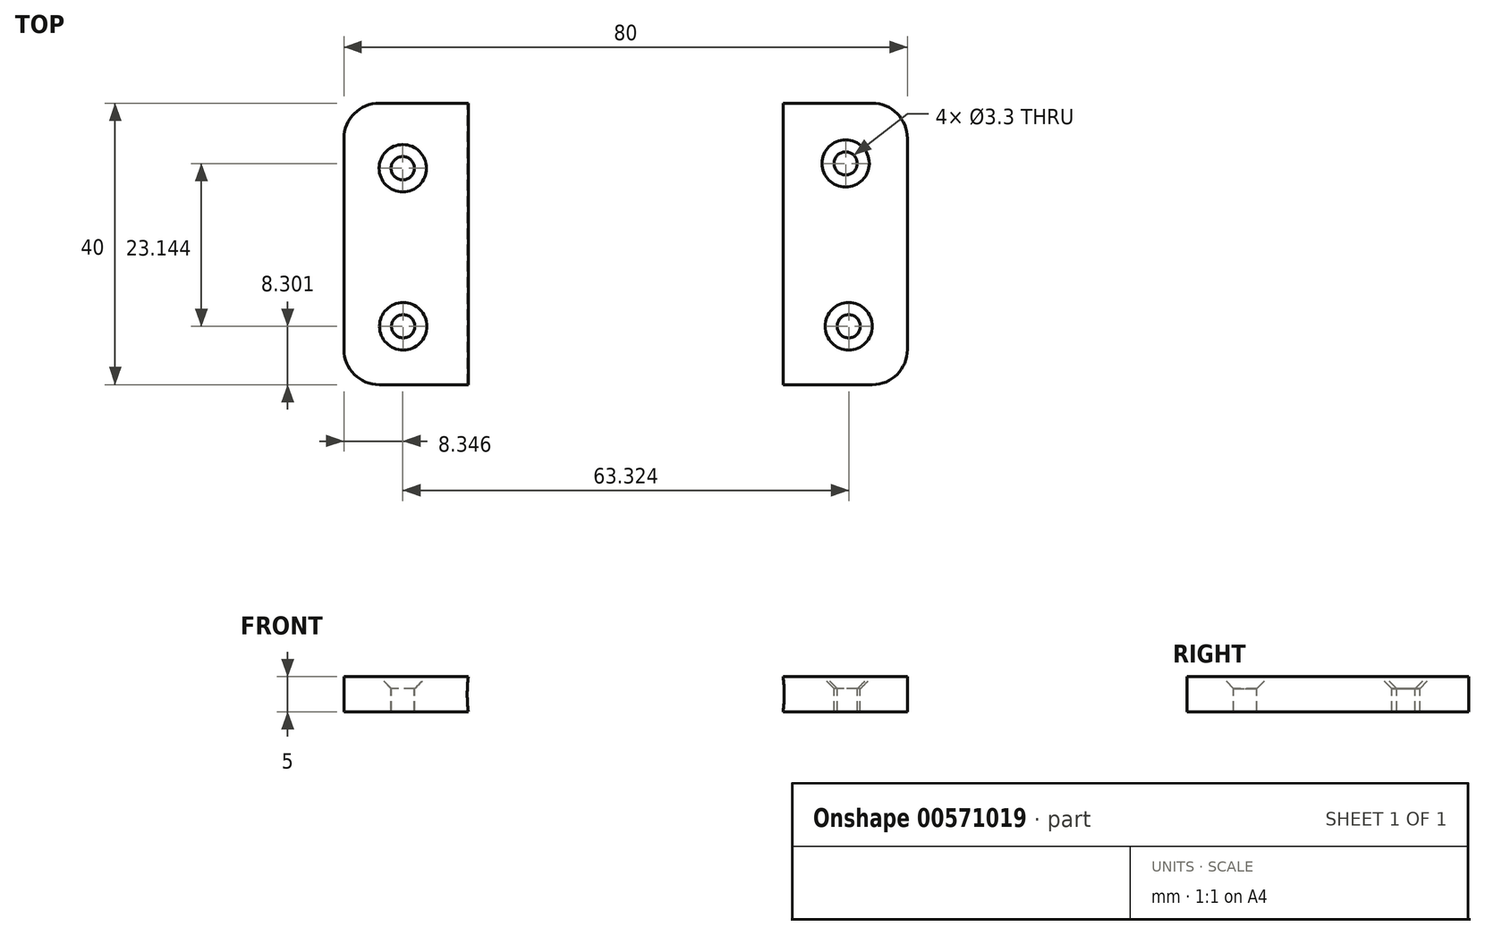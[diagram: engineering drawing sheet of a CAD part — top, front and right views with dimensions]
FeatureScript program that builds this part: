
annotation { "Feature Type Name" : "Feature", "Feature Type Description" : "" }
export const myFeature = defineFeature(function(context is Context, id is Id, definition is map)
    precondition{}
    {
        {
            var Q0;
            Q0=qCreatedBy(makeId("Front.planeOp"),FACE);
            var sketch = newSketch(context, id + "F0", { "sketchPlane" : qUnion([Q0])});
            skLineSegment(sketch, "E0.bottom", {"start": v(40, -2.5) * mm, "end": v(-40, -2.5) * mm});
            skLineSegment(sketch, "E0.top", {"start": v(40, 2.5) * mm, "end": v(-40, 2.5) * mm});
            skLineSegment(sketch, "E0.left", {"start": v(40, -2.5) * mm, "end": v(40, 2.5) * mm});
            skLineSegment(sketch, "E0.right", {"start": v(-40, -2.5) * mm, "end": v(-40, 2.5) * mm});
            skPoint(sketch, "E0.middle", {"position": v(0, 0) * mm});
            skCircle(sketch, "E1", {"center": v(0, 0) * mm, "radius": 22.5 * mm});
            skCircle(sketch, "E2", {"center": v(0, 0) * mm, "radius": 17.5 * mm});
            skSolve(sketch);
        }
        {
            var Q0;
            {var subQ0=sQuery(id+"F0.wireOp",EDGE,"E0.right");Q0=makeQuery(id+"F0.imprint","IMPRINT",FACE,{"disambiguationData":[TD([[makeQuery(id+"F0.imprint","IMPRINT",EDGE,{"derivedFrom":subQ0}),-1.0]])]});}
            var Q1;
            {var subQ0=sQuery(id+"F0.wireOp",EDGE,"E1");var subQ1=sQuery(id+"F0.wireOp",EDGE,"E0.bottom");var subQ2=makeQuery(id+"F0.imprint","INTERSECT",VERTEX,{"disambiguationData":[OD(1.0)],"derivedFrom":[subQ1,subQ0]});Q1=makeQuery(id+"F0.imprint","IMPRINT",FACE,{"disambiguationData":[TD([[makeQuery(id+"F0.imprint","IMPRINT",EDGE,{"disambiguationData":[TD([[subQ2,1.0]])],"derivedFrom":subQ1}),-1.0]])]});}
            var Q2;
            {var subQ0=sQuery(id+"F0.wireOp",EDGE,"E1");var subQ1=sQuery(id+"F0.wireOp",EDGE,"E0.top");var subQ2=makeQuery(id+"F0.imprint","INTERSECT",VERTEX,{"disambiguationData":[OD(0.0)],"derivedFrom":[subQ1,subQ0]});Q2=makeQuery(id+"F0.imprint","IMPRINT",FACE,{"disambiguationData":[TD([[makeQuery(id+"F0.imprint","IMPRINT",EDGE,{"disambiguationData":[TD([[subQ2,-1.0]])],"derivedFrom":subQ1}),-1.0]])]});}
            var Q3;
            {var subQ0=sQuery(id+"F0.wireOp",EDGE,"E1");var subQ1=sQuery(id+"F0.wireOp",EDGE,"E0.bottom");var subQ2=makeQuery(id+"F0.imprint","INTERSECT",VERTEX,{"disambiguationData":[OD(0.0)],"derivedFrom":[subQ1,subQ0]});Q3=makeQuery(id+"F0.imprint","IMPRINT",FACE,{"disambiguationData":[TD([[makeQuery(id+"F0.imprint","IMPRINT",EDGE,{"disambiguationData":[TD([[subQ2,-1.0]])],"derivedFrom":subQ1}),-1.0]])]});}
            var Q4;
            {var subQ0=sQuery(id+"F0.wireOp",EDGE,"E0.left");Q4=makeQuery(id+"F0.imprint","IMPRINT",FACE,{"disambiguationData":[TD([[makeQuery(id+"F0.imprint","IMPRINT",EDGE,{"derivedFrom":subQ0}),1.0]])]});}
            extrude(context, id + "F1", {"entities" : qUnion([Q0, Q1, Q2, Q3, Q4]), "depth" : 40 * mm, "offsetDistance" : 25 * mm});
        }
        {
            var Q0;
            Q0=makeQuery(id+"F1.opExtrude","CAP_EDGE",EDGE,{"disambiguationData":[OSD([sQuery(id+"F0.wireOp",EDGE,"E0.right")])],"isStart":false});
            var Q1;
            Q1=makeQuery(id+"F1.opExtrude","CAP_EDGE",EDGE,{"disambiguationData":[OSD([sQuery(id+"F0.wireOp",EDGE,"E0.right")])],"isStart":true});
            var Q2;
            Q2=makeQuery(id+"F1.opExtrude","CAP_EDGE",EDGE,{"disambiguationData":[OSD([sQuery(id+"F0.wireOp",EDGE,"E0.left")])],"isStart":false});
            var Q3;
            Q3=makeQuery(id+"F1.opExtrude","CAP_EDGE",EDGE,{"disambiguationData":[OSD([sQuery(id+"F0.wireOp",EDGE,"E0.left")])],"isStart":true});
            fillet(context, id + "F2", {"entities" : qUnion([Q0, Q1, Q2, Q3]), "radius" : 5 * mm, "tangentPropagation" : true, "allowEdgeOverflow" : false});
        }
        {
            var Q0;
            {var subQ0=sQuery(id+"F0.wireOp",EDGE,"E0.top");Q0=makeQuery(id+"F1.opExtrude","SWEPT_FACE",FACE,{"disambiguationData":[OSD([subQ0]),TDD([makeQuery(id+"F0.imprint","IMPRINT",EDGE,{"disambiguationData":[TD([[makeQuery(id+"F0.imprint","INTERSECT",VERTEX,{"derivedFrom":[subQ0,sQuery(id+"F0.wireOp",EDGE,"E0.right")]}),1.0]])],"derivedFrom":subQ0})])]});}
            var sketch = newSketch(context, id + "F3", { "sketchPlane" : qUnion([Q0])});
            skPoint(sketch, "E3", {"position": v(-31.65, -9.23) * mm});
            skPoint(sketch, "E4", {"position": v(-31.6, -31.7) * mm});
            skPoint(sketch, "E5", {"position": v(31.23, -8.56) * mm});
            skPoint(sketch, "E6", {"position": v(31.67, -31.7) * mm});
            skSolve(sketch);
        }
        {
            var Q0;
            Q0=sQuery(id+"F3.wireOp",VERTEX,"E3");
            var Q1;
            Q1=sQuery(id+"F3.wireOp",VERTEX,"E4");
            var Q2;
            Q2=sQuery(id+"F3.wireOp",VERTEX,"E5");
            var Q3;
            Q3=sQuery(id+"F3.wireOp",VERTEX,"E6");
            var Q4;
            Q4=makeQuery(id+"F1.opExtrude","SWEPT_BODY",BODY,{"disambiguationData":[OSD([sQuery(id+"F0.wireOp",EDGE,"E0.bottom"),sQuery(id+"F0.wireOp",EDGE,"E0.top"),sQuery(id+"F0.wireOp",EDGE,"E0.left"),sQuery(id+"F0.wireOp",EDGE,"E0.right"),sQuery(id+"F0.wireOp",EDGE,"E1"),sQuery(id+"F0.wireOp",EDGE,"E2")])]});
            hole(context, id + "F4", {"style" : HoleStyle.C_SINK, "endStyle" : HoleEndStyle.BLIND, "standardTappedOrClearance" : lookupTablePath({ "standard" : "ISO", "fit" : "Normal", "size" : "M3", "type" : "Clearance" }), "standardBlindInLast" : lookupTablePath({ "fit" : "Standard", "standard" : "ISO", "size" : "M3", "type" : "Clearance" }), "holeDiameter" : 3.3 * mm, "cSinkDiameter" : 6.72 * mm, "cSinkAngle" : 90 * degree, "holeDepth" : 13.5 * mm, "isTappedThrough" : true, "tappedDepth" : 12 * mm, "tapClearance" : 3, "locations" : qUnion([Q0, Q1, Q2, Q3]), "scope" : qUnion([Q4])});
        }
    });
